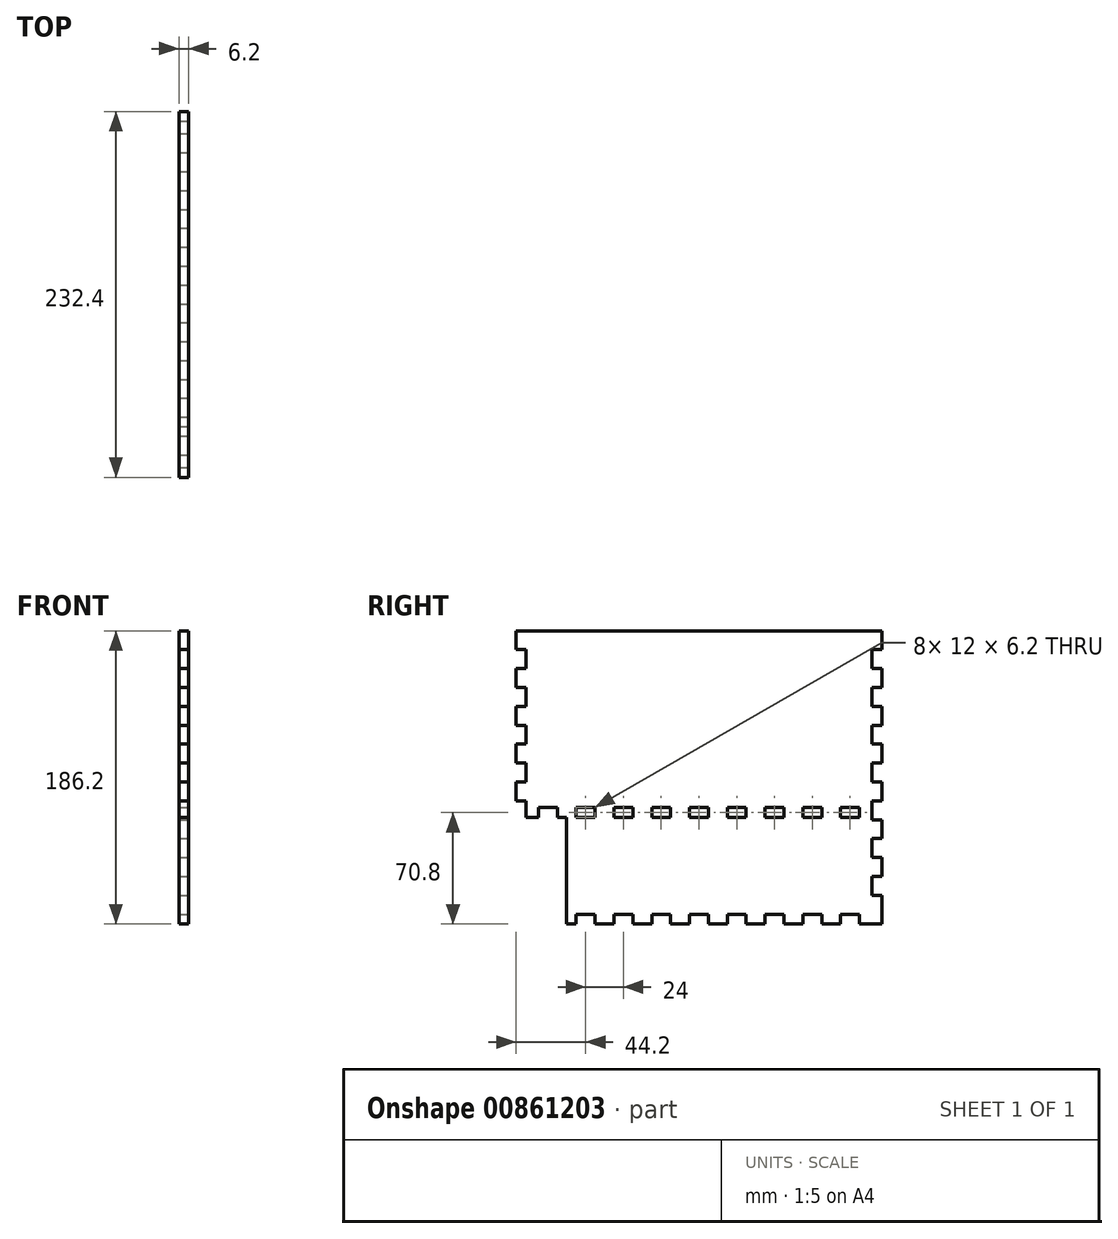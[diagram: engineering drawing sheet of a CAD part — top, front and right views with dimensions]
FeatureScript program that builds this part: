
annotation { "Feature Type Name" : "Feature", "Feature Type Description" : "" }
export const myFeature = defineFeature(function(context is Context, id is Id, definition is map)
    precondition{}
    {
        {
            var Q0;
            Q0=qCreatedBy(makeId("Right.planeOp"),FACE);
            var sketch = newSketch(context, id + "F0", { "sketchPlane" : qUnion([Q0])});
            skLineSegment(sketch, "E0.bottom", {"start": v(110, 90) * mm, "end": v(-110, 90) * mm});
            skLineSegment(sketch, "E0.top", {"start": v(110, -90) * mm, "end": v(-110, -90) * mm});
            skLineSegment(sketch, "E0.left", {"start": v(110, 90) * mm, "end": v(110, -90) * mm});
            skLineSegment(sketch, "E0.right", {"start": v(-110, 90) * mm, "end": v(-110, -90) * mm});
            skPoint(sketch, "E0.middle", {"position": v(0, 0) * mm});
            skSolve(sketch);
        }
        {
            var Q0;
            Q0=makeQuery(id+"F0.imprint","IMPRINT",FACE,{"disambiguationData":[TD([[makeQuery(id+"F0.imprint","IMPRINT",EDGE,{"derivedFrom":sQuery(id+"F0.wireOp",EDGE,"E0.bottom")}),1.0]])]});
            extrude(context, id + "F1", {"entities" : qUnion([Q0]), "depth" : 6.2 * mm, "offsetDistance" : 25 * mm});
        }
        {
            var Q0;
            Q0=makeQuery(id+"F1.opExtrude","CAP_FACE",FACE,{"disambiguationData":[OSD([sQuery(id+"F0.wireOp",EDGE,"E0.bottom"),sQuery(id+"F0.wireOp",EDGE,"E0.top"),sQuery(id+"F0.wireOp",EDGE,"E0.left"),sQuery(id+"F0.wireOp",EDGE,"E0.right")])],"isStart":false});
            var sketch = newSketch(context, id + "F2", { "sketchPlane" : qUnion([Q0])});
            skLineSegment(sketch, "E1", {"start": v(-110, -90) * mm, "end": v(-110, -28.5) * mm, "construction": true});
            skLineSegment(sketch, "E2", {"start": v(-110, -28.5) * mm, "end": v(0, -28.5) * mm, "construction": true});
            skLineSegment(sketch, "E3", {"start": v(0, -28.5) * mm, "end": v(0, -22.3) * mm, "construction": true});
            skPoint(sketch, "E4.orphan", {"position": v(110, -28.5) * mm});
            skLineSegment(sketch, "E5.bottom", {"start": v(6, -22.3) * mm, "end": v(-6, -22.3) * mm});
            skLineSegment(sketch, "E5.top", {"start": v(6, -28.5) * mm, "end": v(-6, -28.5) * mm});
            skLineSegment(sketch, "E5.left", {"start": v(6, -22.3) * mm, "end": v(6, -28.5) * mm});
            skLineSegment(sketch, "E5.right", {"start": v(-6, -22.3) * mm, "end": v(-6, -28.5) * mm});
            skPoint(sketch, "E5.middle", {"position": v(0, -25.4) * mm});
            skLineSegment(sketch, "E6.1.0.0", {"start": v(30, -28.5) * mm, "end": v(18, -28.5) * mm});
            skLineSegment(sketch, "E6.1.0.1", {"start": v(30, -22.3) * mm, "end": v(30, -28.5) * mm});
            skLineSegment(sketch, "E6.1.0.2", {"start": v(30, -22.3) * mm, "end": v(18, -22.3) * mm});
            skLineSegment(sketch, "E6.1.0.3", {"start": v(18, -22.3) * mm, "end": v(18, -28.5) * mm});
            skLineSegment(sketch, "E6.2.0.0", {"start": v(54, -28.5) * mm, "end": v(42, -28.5) * mm});
            skLineSegment(sketch, "E6.2.0.1", {"start": v(54, -22.3) * mm, "end": v(54, -28.5) * mm});
            skLineSegment(sketch, "E6.2.0.2", {"start": v(54, -22.3) * mm, "end": v(42, -22.3) * mm});
            skLineSegment(sketch, "E6.2.0.3", {"start": v(42, -22.3) * mm, "end": v(42, -28.5) * mm});
            skLineSegment(sketch, "E6.3.0.0", {"start": v(78, -28.5) * mm, "end": v(66, -28.5) * mm});
            skLineSegment(sketch, "E6.3.0.1", {"start": v(78, -22.3) * mm, "end": v(78, -28.5) * mm});
            skLineSegment(sketch, "E6.3.0.2", {"start": v(78, -22.3) * mm, "end": v(66, -22.3) * mm});
            skLineSegment(sketch, "E6.3.0.3", {"start": v(66, -22.3) * mm, "end": v(66, -28.5) * mm});
            skLineSegment(sketch, "E6.4.0.0", {"start": v(102, -28.5) * mm, "end": v(90, -28.5) * mm});
            skLineSegment(sketch, "E6.4.0.1", {"start": v(102, -22.3) * mm, "end": v(102, -28.5) * mm});
            skLineSegment(sketch, "E6.4.0.2", {"start": v(102, -22.3) * mm, "end": v(90, -22.3) * mm});
            skLineSegment(sketch, "E6.4.0.3", {"start": v(90, -22.3) * mm, "end": v(90, -28.5) * mm});
            skLineSegment(sketch, "E6.direction1", {"start": v(-6, -28.5) * mm, "end": v(18, -28.5) * mm, "construction": true});
            skLineSegment(sketch, "E7.MirrorCS", {"start": v(-78, -22.3) * mm, "end": v(-78, -28.5) * mm});
            skLineSegment(sketch, "E8.MirrorCS", {"start": v(-66, -22.3) * mm, "end": v(-66, -28.5) * mm});
            skLineSegment(sketch, "E9.MirrorCS", {"start": v(-102, -22.3) * mm, "end": v(-102, -28.5) * mm});
            skLineSegment(sketch, "E10.MirrorCS", {"start": v(-30, -22.3) * mm, "end": v(-30, -28.5) * mm});
            skLineSegment(sketch, "E11.MirrorCS", {"start": v(-42, -22.3) * mm, "end": v(-42, -28.5) * mm});
            skLineSegment(sketch, "E12.MirrorCS", {"start": v(-18, -22.3) * mm, "end": v(-18, -28.5) * mm});
            skLineSegment(sketch, "E13.MirrorCS", {"start": v(-54, -22.3) * mm, "end": v(-54, -28.5) * mm});
            skLineSegment(sketch, "E14.MirrorCS", {"start": v(-90, -22.3) * mm, "end": v(-90, -28.5) * mm});
            skLineSegment(sketch, "E15.MirrorCS", {"start": v(-78, -22.3) * mm, "end": v(-66, -22.3) * mm});
            skLineSegment(sketch, "E16.MirrorCS", {"start": v(-102, -28.5) * mm, "end": v(-90, -28.5) * mm});
            skLineSegment(sketch, "E17.MirrorCS", {"start": v(-102, -22.3) * mm, "end": v(-90, -22.3) * mm});
            skLineSegment(sketch, "E18.MirrorCS", {"start": v(-30, -28.5) * mm, "end": v(-18, -28.5) * mm});
            skLineSegment(sketch, "E19.MirrorCS", {"start": v(-54, -22.3) * mm, "end": v(-42, -22.3) * mm});
            skLineSegment(sketch, "E20.MirrorCS", {"start": v(-54, -28.5) * mm, "end": v(-42, -28.5) * mm});
            skLineSegment(sketch, "E21.MirrorCS", {"start": v(-30, -22.3) * mm, "end": v(-18, -22.3) * mm});
            skLineSegment(sketch, "E22.MirrorCS", {"start": v(-78, -28.5) * mm, "end": v(-66, -28.5) * mm});
            skSolve(sketch);
        }
        {
            var Q0;
            Q0=makeQuery(id+"F2.imprint","IMPRINT",FACE,{"disambiguationData":[TD([[makeQuery(id+"F2.imprint","IMPRINT",EDGE,{"derivedFrom":sQuery(id+"F2.wireOp",EDGE,"E9.MirrorCS")}),1.0]])]});
            var Q1;
            Q1=makeQuery(id+"F2.imprint","IMPRINT",FACE,{"disambiguationData":[TD([[makeQuery(id+"F2.imprint","IMPRINT",EDGE,{"derivedFrom":sQuery(id+"F2.wireOp",EDGE,"E7.MirrorCS")}),1.0]])]});
            var Q2;
            Q2=makeQuery(id+"F2.imprint","IMPRINT",FACE,{"disambiguationData":[TD([[makeQuery(id+"F2.imprint","IMPRINT",EDGE,{"derivedFrom":sQuery(id+"F2.wireOp",EDGE,"E11.MirrorCS")}),-1.0]])]});
            var Q3;
            Q3=makeQuery(id+"F2.imprint","IMPRINT",FACE,{"disambiguationData":[TD([[makeQuery(id+"F2.imprint","IMPRINT",EDGE,{"derivedFrom":sQuery(id+"F2.wireOp",EDGE,"E10.MirrorCS")}),1.0]])]});
            var Q4;
            Q4=makeQuery(id+"F2.imprint","IMPRINT",FACE,{"disambiguationData":[TD([[makeQuery(id+"F2.imprint","IMPRINT",EDGE,{"derivedFrom":sQuery(id+"F2.wireOp",EDGE,"E5.bottom")}),1.0]])]});
            var Q5;
            Q5=makeQuery(id+"F2.imprint","IMPRINT",FACE,{"disambiguationData":[TD([[makeQuery(id+"F2.imprint","IMPRINT",EDGE,{"derivedFrom":sQuery(id+"F2.wireOp",EDGE,"E6.1.0.0")}),-1.0]])]});
            var Q6;
            Q6=makeQuery(id+"F2.imprint","IMPRINT",FACE,{"disambiguationData":[TD([[makeQuery(id+"F2.imprint","IMPRINT",EDGE,{"derivedFrom":sQuery(id+"F2.wireOp",EDGE,"E6.2.0.0")}),-1.0]])]});
            var Q7;
            Q7=makeQuery(id+"F2.imprint","IMPRINT",FACE,{"disambiguationData":[TD([[makeQuery(id+"F2.imprint","IMPRINT",EDGE,{"derivedFrom":sQuery(id+"F2.wireOp",EDGE,"E6.3.0.0")}),-1.0]])]});
            var Q8;
            Q8=makeQuery(id+"F2.imprint","IMPRINT",FACE,{"disambiguationData":[TD([[makeQuery(id+"F2.imprint","IMPRINT",EDGE,{"derivedFrom":sQuery(id+"F2.wireOp",EDGE,"E6.4.0.0")}),-1.0]])]});
            extrude(context, id + "F3", {"entities" : qUnion([Q0, Q1, Q2, Q3, Q4, Q5, Q6, Q7, Q8]), "operationType" : NewBodyOperationType.REMOVE, "endBound" : BoundingType.THROUGH_ALL, "oppositeDirection" : true, "depth" : 25 * mm, "offsetDistance" : 25 * mm});
        }
        {
            var Q0;
            Q0=makeQuery(id+"F1.opExtrude","CAP_FACE",FACE,{"disambiguationData":[OSD([sQuery(id+"F0.wireOp",EDGE,"E0.bottom"),sQuery(id+"F0.wireOp",EDGE,"E0.top"),sQuery(id+"F0.wireOp",EDGE,"E0.left"),sQuery(id+"F0.wireOp",EDGE,"E0.right")])],"isStart":false});
            var sketch = newSketch(context, id + "F4", { "sketchPlane" : qUnion([Q0])});
            skPoint(sketch, "E23.start.orphan", {"position": v(-86, -28.5) * mm});
            skLineSegment(sketch, "E24", {"start": v(-90, -28.5) * mm, "end": v(-78, -28.5) * mm, "construction": true});
            skLineSegment(sketch, "E25.bottom", {"start": v(-84, -28.5) * mm, "end": v(-110, -28.5) * mm});
            skLineSegment(sketch, "E25.top", {"start": v(-84, -90) * mm, "end": v(-110, -90) * mm});
            skLineSegment(sketch, "E25.left", {"start": v(-84, -28.5) * mm, "end": v(-84, -90) * mm});
            skLineSegment(sketch, "E25.right", {"start": v(-110, -28.5) * mm, "end": v(-110, -90) * mm});
            skSolve(sketch);
        }
        {
            var Q0;
            Q0=makeQuery(id+"F4.imprint","IMPRINT",FACE,{"disambiguationData":[TD([[makeQuery(id+"F4.imprint","IMPRINT",EDGE,{"derivedFrom":sQuery(id+"F4.wireOp",EDGE,"E25.top")}),-1.0]])]});
            extrude(context, id + "F5", {"entities" : qUnion([Q0]), "operationType" : NewBodyOperationType.REMOVE, "endBound" : BoundingType.THROUGH_ALL, "oppositeDirection" : true, "depth" : 25 * mm, "offsetDistance" : 25 * mm});
        }
        {
            var Q0;
            Q0=makeQuery(id+"F1.opExtrude","CAP_FACE",FACE,{"disambiguationData":[OSD([sQuery(id+"F0.wireOp",EDGE,"E0.bottom"),sQuery(id+"F0.wireOp",EDGE,"E0.top"),sQuery(id+"F0.wireOp",EDGE,"E0.left"),sQuery(id+"F0.wireOp",EDGE,"E0.right")])],"isStart":false});
            var sketch = newSketch(context, id + "F6", { "sketchPlane" : qUnion([Q0])});
            skLineSegment(sketch, "E26", {"start": v(0, 0) * mm, "end": v(110, 0) * mm, "construction": true});
            skLineSegment(sketch, "E27", {"start": v(110, 0) * mm, "end": v(110, 6) * mm, "construction": true});
            skLineSegment(sketch, "E28.bottom", {"start": v(110, 6) * mm, "end": v(116.2, 6) * mm});
            skLineSegment(sketch, "E28.top", {"start": v(110, 18) * mm, "end": v(116.2, 18) * mm});
            skLineSegment(sketch, "E28.left", {"start": v(110, 6) * mm, "end": v(110, 18) * mm});
            skLineSegment(sketch, "E28.right", {"start": v(116.2, 6) * mm, "end": v(116.2, 18) * mm});
            skLineSegment(sketch, "E29.0.1.0", {"start": v(116.2, 30) * mm, "end": v(116.2, 42) * mm});
            skLineSegment(sketch, "E29.0.1.1", {"start": v(110, 42) * mm, "end": v(116.2, 42) * mm});
            skLineSegment(sketch, "E29.0.1.2", {"start": v(110, 30) * mm, "end": v(110, 42) * mm});
            skLineSegment(sketch, "E29.0.1.3", {"start": v(110, 30) * mm, "end": v(116.2, 30) * mm});
            skLineSegment(sketch, "E29.0.2.0", {"start": v(116.2, 54) * mm, "end": v(116.2, 66) * mm});
            skLineSegment(sketch, "E29.0.2.1", {"start": v(110, 66) * mm, "end": v(116.2, 66) * mm});
            skLineSegment(sketch, "E29.0.2.2", {"start": v(110, 54) * mm, "end": v(110, 66) * mm});
            skLineSegment(sketch, "E29.0.2.3", {"start": v(110, 54) * mm, "end": v(116.2, 54) * mm});
            skLineSegment(sketch, "E29.0.3.0", {"start": v(116.2, 78) * mm, "end": v(116.2, 90) * mm});
            skLineSegment(sketch, "E29.0.3.1", {"start": v(110, 90) * mm, "end": v(116.2, 90) * mm});
            skLineSegment(sketch, "E29.0.3.2", {"start": v(110, 78) * mm, "end": v(110, 90) * mm});
            skLineSegment(sketch, "E29.0.3.3", {"start": v(110, 78) * mm, "end": v(116.2, 78) * mm});
            skLineSegment(sketch, "E29.direction1", {"start": v(116.2, 6) * mm, "end": v(141.2, 6) * mm, "construction": true});
            skLineSegment(sketch, "E29.direction2", {"start": v(116.2, 6) * mm, "end": v(116.2, 30) * mm, "construction": true});
            skLineSegment(sketch, "E30.MirrorCS", {"start": v(116.2, -6) * mm, "end": v(116.2, -18) * mm});
            skLineSegment(sketch, "E31.MirrorCS", {"start": v(110, -42) * mm, "end": v(116.2, -42) * mm});
            skLineSegment(sketch, "E32.MirrorCS", {"start": v(116.2, -6) * mm, "end": v(116.2, -30) * mm, "construction": true});
            skLineSegment(sketch, "E33.MirrorCS", {"start": v(116.2, -30) * mm, "end": v(116.2, -42) * mm});
            skLineSegment(sketch, "E34.MirrorCS", {"start": v(110, -54) * mm, "end": v(110, -66) * mm});
            skLineSegment(sketch, "E35.MirrorCS", {"start": v(116.2, -78) * mm, "end": v(116.2, -90) * mm});
            skLineSegment(sketch, "E36.MirrorCS", {"start": v(110, -66) * mm, "end": v(116.2, -66) * mm});
            skLineSegment(sketch, "E37.MirrorCS", {"start": v(110, -54) * mm, "end": v(116.2, -54) * mm});
            skLineSegment(sketch, "E38.MirrorCS", {"start": v(110, -18) * mm, "end": v(116.2, -18) * mm});
            skLineSegment(sketch, "E39.MirrorCS", {"start": v(110, -6) * mm, "end": v(110, -18) * mm});
            skLineSegment(sketch, "E40.MirrorCS", {"start": v(110, -90) * mm, "end": v(116.2, -90) * mm});
            skLineSegment(sketch, "E41.MirrorCS", {"start": v(110, -78) * mm, "end": v(116.2, -78) * mm});
            skLineSegment(sketch, "E42.MirrorCS", {"start": v(110, -6) * mm, "end": v(116.2, -6) * mm});
            skLineSegment(sketch, "E43.MirrorCS", {"start": v(116.2, -54) * mm, "end": v(116.2, -66) * mm});
            skLineSegment(sketch, "E44.MirrorCS", {"start": v(110, -30) * mm, "end": v(116.2, -30) * mm});
            skLineSegment(sketch, "E45.MirrorCS", {"start": v(110, -30) * mm, "end": v(110, -42) * mm});
            skLineSegment(sketch, "E46.MirrorCS", {"start": v(110, -78) * mm, "end": v(110, -90) * mm});
            skLineSegment(sketch, "E47.MirrorCS", {"start": v(-110, 0) * mm, "end": v(-110, 6) * mm, "construction": true});
            skLineSegment(sketch, "E48.MirrorCS", {"start": v(-110, 6) * mm, "end": v(-116.2, 6) * mm});
            skLineSegment(sketch, "E49.MirrorCS", {"start": v(-110, -6) * mm, "end": v(-116.2, -6) * mm});
            skLineSegment(sketch, "E50.MirrorCS", {"start": v(-110, 30) * mm, "end": v(-116.2, 30) * mm});
            skLineSegment(sketch, "E51.MirrorCS", {"start": v(-110, 42) * mm, "end": v(-116.2, 42) * mm});
            skLineSegment(sketch, "E52.MirrorCS", {"start": v(-116.2, 6) * mm, "end": v(-116.2, 30) * mm, "construction": true});
            skLineSegment(sketch, "E53.MirrorCS", {"start": v(-116.2, 30) * mm, "end": v(-116.2, 42) * mm});
            skLineSegment(sketch, "E54.MirrorCS", {"start": v(-116.2, -6) * mm, "end": v(-116.2, -18) * mm});
            skLineSegment(sketch, "E55.MirrorCS", {"start": v(-110, -6) * mm, "end": v(-110, -18) * mm});
            skLineSegment(sketch, "E56.MirrorCS", {"start": v(-116.2, 6) * mm, "end": v(-116.2, 18) * mm});
            skLineSegment(sketch, "E57.MirrorCS", {"start": v(-110, 30) * mm, "end": v(-110, 42) * mm});
            skLineSegment(sketch, "E58.MirrorCS", {"start": v(-116.2, 78) * mm, "end": v(-116.2, 90) * mm});
            skLineSegment(sketch, "E59.MirrorCS", {"start": v(-110, 54) * mm, "end": v(-116.2, 54) * mm});
            skLineSegment(sketch, "E60.MirrorCS", {"start": v(-110, 66) * mm, "end": v(-116.2, 66) * mm});
            skLineSegment(sketch, "E61.MirrorCS", {"start": v(-116.2, 54) * mm, "end": v(-116.2, 66) * mm});
            skLineSegment(sketch, "E62.MirrorCS", {"start": v(-110, -18) * mm, "end": v(-116.2, -18) * mm});
            skLineSegment(sketch, "E63.MirrorCS", {"start": v(-110, 18) * mm, "end": v(-116.2, 18) * mm});
            skLineSegment(sketch, "E64.MirrorCS", {"start": v(-110, 54) * mm, "end": v(-110, 66) * mm});
            skLineSegment(sketch, "E65.MirrorCS", {"start": v(-116.2, -6) * mm, "end": v(-116.2, -30) * mm, "construction": true});
            skLineSegment(sketch, "E66.MirrorCS", {"start": v(-110, 78) * mm, "end": v(-110, 90) * mm});
            skLineSegment(sketch, "E67.MirrorCS", {"start": v(-110, 6) * mm, "end": v(-110, 18) * mm});
            skLineSegment(sketch, "E68.MirrorCS", {"start": v(-110, 90) * mm, "end": v(-116.2, 90) * mm});
            skLineSegment(sketch, "E69.MirrorCS", {"start": v(-110, 78) * mm, "end": v(-116.2, 78) * mm});
            skLineSegment(sketch, "E70.MirrorCS", {"start": v(-116.2, 6) * mm, "end": v(-141.2, 6) * mm, "construction": true});
            skPoint(sketch, "E71.MirrorCS.start.orphan", {"position": v(-110, -30) * mm});
            skPoint(sketch, "E72.MirrorCS.end.orphan", {"position": v(-116.2, -42) * mm});
            skPoint(sketch, "E72.MirrorCS.start.orphan", {"position": v(-110, -42) * mm});
            skSolve(sketch);
        }
        {
            var Q0;
            Q0 = qSketchRegion(id + "F6", true);
            extrude(context, id + "F7", {"entities" : qUnion([Q0]), "operationType" : NewBodyOperationType.ADD, "oppositeDirection" : true, "depth" : 6.2 * mm, "offsetDistance" : 25 * mm});
        }
        {
            var Q0;
            Q0=makeQuery(id+"F7.boolean.opBoolean","MERGE",FACE,{"derivedFrom":[makeQuery(id+"F1.opExtrude","CAP_FACE",FACE,{"disambiguationData":[OSD([sQuery(id+"F0.wireOp",EDGE,"E0.bottom"),sQuery(id+"F0.wireOp",EDGE,"E0.top"),sQuery(id+"F0.wireOp",EDGE,"E0.left"),sQuery(id+"F0.wireOp",EDGE,"E0.right")])],"isStart":false}),makeQuery(id+"F7.opExtrude","CAP_FACE",FACE,{"disambiguationData":[OSD([sQuery(id+"F6.wireOp",EDGE,"E28.bottom"),sQuery(id+"F6.wireOp",EDGE,"E28.top"),sQuery(id+"F6.wireOp",EDGE,"E28.left"),sQuery(id+"F6.wireOp",EDGE,"E28.right")])],"isStart":true}),makeQuery(id+"F7.opExtrude","CAP_FACE",FACE,{"disambiguationData":[OSD([sQuery(id+"F6.wireOp",EDGE,"E29.0.1.0"),sQuery(id+"F6.wireOp",EDGE,"E29.0.1.1"),sQuery(id+"F6.wireOp",EDGE,"E29.0.1.2"),sQuery(id+"F6.wireOp",EDGE,"E29.0.1.3")])],"isStart":true}),makeQuery(id+"F7.opExtrude","CAP_FACE",FACE,{"disambiguationData":[OSD([sQuery(id+"F6.wireOp",EDGE,"E29.0.2.0"),sQuery(id+"F6.wireOp",EDGE,"E29.0.2.1"),sQuery(id+"F6.wireOp",EDGE,"E29.0.2.2"),sQuery(id+"F6.wireOp",EDGE,"E29.0.2.3")])],"isStart":true}),makeQuery(id+"F7.opExtrude","CAP_FACE",FACE,{"disambiguationData":[OSD([sQuery(id+"F6.wireOp",EDGE,"E29.0.3.0"),sQuery(id+"F6.wireOp",EDGE,"E29.0.3.1"),sQuery(id+"F6.wireOp",EDGE,"E29.0.3.2"),sQuery(id+"F6.wireOp",EDGE,"E29.0.3.3")])],"isStart":true}),makeQuery(id+"F7.opExtrude","CAP_FACE",FACE,{"disambiguationData":[OSD([sQuery(id+"F6.wireOp",EDGE,"E30.MirrorCS"),sQuery(id+"F6.wireOp",EDGE,"E38.MirrorCS"),sQuery(id+"F6.wireOp",EDGE,"E39.MirrorCS"),sQuery(id+"F6.wireOp",EDGE,"E42.MirrorCS")])],"isStart":true}),makeQuery(id+"F7.opExtrude","CAP_FACE",FACE,{"disambiguationData":[OSD([sQuery(id+"F6.wireOp",EDGE,"E31.MirrorCS"),sQuery(id+"F6.wireOp",EDGE,"E33.MirrorCS"),sQuery(id+"F6.wireOp",EDGE,"E44.MirrorCS"),sQuery(id+"F6.wireOp",EDGE,"E45.MirrorCS")])],"isStart":true}),makeQuery(id+"F7.opExtrude","CAP_FACE",FACE,{"disambiguationData":[OSD([sQuery(id+"F6.wireOp",EDGE,"E34.MirrorCS"),sQuery(id+"F6.wireOp",EDGE,"E36.MirrorCS"),sQuery(id+"F6.wireOp",EDGE,"E37.MirrorCS"),sQuery(id+"F6.wireOp",EDGE,"E43.MirrorCS")])],"isStart":true}),makeQuery(id+"F7.opExtrude","CAP_FACE",FACE,{"disambiguationData":[OSD([sQuery(id+"F6.wireOp",EDGE,"E35.MirrorCS"),sQuery(id+"F6.wireOp",EDGE,"E40.MirrorCS"),sQuery(id+"F6.wireOp",EDGE,"E41.MirrorCS"),sQuery(id+"F6.wireOp",EDGE,"E46.MirrorCS")])],"isStart":true}),makeQuery(id+"F7.opExtrude","CAP_FACE",FACE,{"disambiguationData":[OSD([sQuery(id+"F6.wireOp",EDGE,"E48.MirrorCS"),sQuery(id+"F6.wireOp",EDGE,"E56.MirrorCS"),sQuery(id+"F6.wireOp",EDGE,"E63.MirrorCS"),sQuery(id+"F6.wireOp",EDGE,"E67.MirrorCS")])],"isStart":true}),makeQuery(id+"F7.opExtrude","CAP_FACE",FACE,{"disambiguationData":[OSD([sQuery(id+"F6.wireOp",EDGE,"E49.MirrorCS"),sQuery(id+"F6.wireOp",EDGE,"E54.MirrorCS"),sQuery(id+"F6.wireOp",EDGE,"E55.MirrorCS"),sQuery(id+"F6.wireOp",EDGE,"E62.MirrorCS")])],"isStart":true}),makeQuery(id+"F7.opExtrude","CAP_FACE",FACE,{"disambiguationData":[OSD([sQuery(id+"F6.wireOp",EDGE,"E50.MirrorCS"),sQuery(id+"F6.wireOp",EDGE,"E51.MirrorCS"),sQuery(id+"F6.wireOp",EDGE,"E53.MirrorCS"),sQuery(id+"F6.wireOp",EDGE,"E57.MirrorCS")])],"isStart":true}),makeQuery(id+"F7.opExtrude","CAP_FACE",FACE,{"disambiguationData":[OSD([sQuery(id+"F6.wireOp",EDGE,"E58.MirrorCS"),sQuery(id+"F6.wireOp",EDGE,"E66.MirrorCS"),sQuery(id+"F6.wireOp",EDGE,"E68.MirrorCS"),sQuery(id+"F6.wireOp",EDGE,"E69.MirrorCS")])],"isStart":true}),makeQuery(id+"F7.opExtrude","CAP_FACE",FACE,{"disambiguationData":[OSD([sQuery(id+"F6.wireOp",EDGE,"E59.MirrorCS"),sQuery(id+"F6.wireOp",EDGE,"E60.MirrorCS"),sQuery(id+"F6.wireOp",EDGE,"E61.MirrorCS"),sQuery(id+"F6.wireOp",EDGE,"E64.MirrorCS")])],"isStart":true})]});
            var sketch = newSketch(context, id + "F8", { "sketchPlane" : qUnion([Q0])});
            skLineSegment(sketch, "E73.bottom", {"start": v(-84, -90) * mm, "end": v(-78, -90) * mm});
            skLineSegment(sketch, "E73.top", {"start": v(-84, -96.2) * mm, "end": v(-78, -96.2) * mm});
            skLineSegment(sketch, "E73.left", {"start": v(-84, -90) * mm, "end": v(-84, -96.2) * mm});
            skLineSegment(sketch, "E73.right", {"start": v(-78, -90) * mm, "end": v(-78, -96.2) * mm});
            skLineSegment(sketch, "E74", {"start": v(-78, -90) * mm, "end": v(-66, -90) * mm, "construction": true});
            skLineSegment(sketch, "E75.bottom", {"start": v(-66, -90) * mm, "end": v(-54, -90) * mm});
            skLineSegment(sketch, "E75.top", {"start": v(-66, -96.2) * mm, "end": v(-54, -96.2) * mm});
            skLineSegment(sketch, "E75.left", {"start": v(-66, -90) * mm, "end": v(-66, -96.2) * mm});
            skLineSegment(sketch, "E75.right", {"start": v(-54, -90) * mm, "end": v(-54, -96.2) * mm});
            skLineSegment(sketch, "E76.1.0.0", {"start": v(-42, -96.2) * mm, "end": v(-30, -96.2) * mm});
            skLineSegment(sketch, "E76.1.0.1", {"start": v(-30, -90) * mm, "end": v(-30, -96.2) * mm});
            skLineSegment(sketch, "E76.1.0.2", {"start": v(-42, -90) * mm, "end": v(-30, -90) * mm});
            skLineSegment(sketch, "E76.1.0.3", {"start": v(-42, -90) * mm, "end": v(-42, -96.2) * mm});
            skLineSegment(sketch, "E76.1.0.4", {"start": v(-54, -90) * mm, "end": v(-42, -90) * mm, "construction": true});
            skLineSegment(sketch, "E76.2.0.0", {"start": v(-18, -96.2) * mm, "end": v(-6, -96.2) * mm});
            skLineSegment(sketch, "E76.2.0.1", {"start": v(-6, -90) * mm, "end": v(-6, -96.2) * mm});
            skLineSegment(sketch, "E76.2.0.2", {"start": v(-18, -90) * mm, "end": v(-6, -90) * mm});
            skLineSegment(sketch, "E76.2.0.3", {"start": v(-18, -90) * mm, "end": v(-18, -96.2) * mm});
            skLineSegment(sketch, "E76.2.0.4", {"start": v(-30, -90) * mm, "end": v(-18, -90) * mm, "construction": true});
            skLineSegment(sketch, "E76.3.0.0", {"start": v(6, -96.2) * mm, "end": v(18, -96.2) * mm});
            skLineSegment(sketch, "E76.3.0.1", {"start": v(18, -90) * mm, "end": v(18, -96.2) * mm});
            skLineSegment(sketch, "E76.3.0.2", {"start": v(6, -90) * mm, "end": v(18, -90) * mm});
            skLineSegment(sketch, "E76.3.0.3", {"start": v(6, -90) * mm, "end": v(6, -96.2) * mm});
            skLineSegment(sketch, "E76.3.0.4", {"start": v(-6, -90) * mm, "end": v(6, -90) * mm, "construction": true});
            skLineSegment(sketch, "E76.4.0.0", {"start": v(30, -96.2) * mm, "end": v(42, -96.2) * mm});
            skLineSegment(sketch, "E76.4.0.1", {"start": v(42, -90) * mm, "end": v(42, -96.2) * mm});
            skLineSegment(sketch, "E76.4.0.2", {"start": v(30, -90) * mm, "end": v(42, -90) * mm});
            skLineSegment(sketch, "E76.4.0.3", {"start": v(30, -90) * mm, "end": v(30, -96.2) * mm});
            skLineSegment(sketch, "E76.4.0.4", {"start": v(18, -90) * mm, "end": v(30, -90) * mm, "construction": true});
            skLineSegment(sketch, "E76.5.0.0", {"start": v(54, -96.2) * mm, "end": v(66, -96.2) * mm});
            skLineSegment(sketch, "E76.5.0.1", {"start": v(66, -90) * mm, "end": v(66, -96.2) * mm});
            skLineSegment(sketch, "E76.5.0.2", {"start": v(54, -90) * mm, "end": v(66, -90) * mm});
            skLineSegment(sketch, "E76.5.0.3", {"start": v(54, -90) * mm, "end": v(54, -96.2) * mm});
            skLineSegment(sketch, "E76.5.0.4", {"start": v(42, -90) * mm, "end": v(54, -90) * mm, "construction": true});
            skLineSegment(sketch, "E76.6.0.0", {"start": v(78, -96.2) * mm, "end": v(90, -96.2) * mm});
            skLineSegment(sketch, "E76.6.0.1", {"start": v(90, -90) * mm, "end": v(90, -96.2) * mm});
            skLineSegment(sketch, "E76.6.0.2", {"start": v(78, -90) * mm, "end": v(90, -90) * mm});
            skLineSegment(sketch, "E76.6.0.3", {"start": v(78, -90) * mm, "end": v(78, -96.2) * mm});
            skLineSegment(sketch, "E76.6.0.4", {"start": v(66, -90) * mm, "end": v(78, -90) * mm, "construction": true});
            skLineSegment(sketch, "E76.7.0.0", {"start": v(102, -96.2) * mm, "end": v(114, -96.2) * mm});
            skLineSegment(sketch, "E76.7.0.1", {"start": v(114, -90) * mm, "end": v(114, -96.2) * mm});
            skLineSegment(sketch, "E76.7.0.2", {"start": v(102, -90) * mm, "end": v(114, -90) * mm});
            skLineSegment(sketch, "E76.7.0.3", {"start": v(102, -90) * mm, "end": v(102, -96.2) * mm});
            skLineSegment(sketch, "E76.7.0.4", {"start": v(90, -90) * mm, "end": v(102, -90) * mm, "construction": true});
            skLineSegment(sketch, "E76.direction1", {"start": v(-78, -90) * mm, "end": v(-54, -90) * mm, "construction": true});
            skSolve(sketch);
        }
        {
            var Q0;
            Q0 = qSketchRegion(id + "F8", true);
            extrude(context, id + "F9", {"entities" : qUnion([Q0]), "operationType" : NewBodyOperationType.ADD, "oppositeDirection" : true, "depth" : 6.2 * mm, "offsetDistance" : 25 * mm});
        }
        {
            var Q0;
            Q0=makeQuery(id+"F9.boolean.opBoolean","MERGE",FACE,{"derivedFrom":[makeQuery(id+"F7.boolean.opBoolean","MERGE",FACE,{"derivedFrom":[makeQuery(id+"F1.opExtrude","CAP_FACE",FACE,{"disambiguationData":[OSD([sQuery(id+"F0.wireOp",EDGE,"E0.bottom"),sQuery(id+"F0.wireOp",EDGE,"E0.top"),sQuery(id+"F0.wireOp",EDGE,"E0.left"),sQuery(id+"F0.wireOp",EDGE,"E0.right")])],"isStart":false}),makeQuery(id+"F7.opExtrude","CAP_FACE",FACE,{"disambiguationData":[OSD([sQuery(id+"F6.wireOp",EDGE,"E28.bottom"),sQuery(id+"F6.wireOp",EDGE,"E28.top"),sQuery(id+"F6.wireOp",EDGE,"E28.left"),sQuery(id+"F6.wireOp",EDGE,"E28.right")])],"isStart":true}),makeQuery(id+"F7.opExtrude","CAP_FACE",FACE,{"disambiguationData":[OSD([sQuery(id+"F6.wireOp",EDGE,"E29.0.1.0"),sQuery(id+"F6.wireOp",EDGE,"E29.0.1.1"),sQuery(id+"F6.wireOp",EDGE,"E29.0.1.2"),sQuery(id+"F6.wireOp",EDGE,"E29.0.1.3")])],"isStart":true}),makeQuery(id+"F7.opExtrude","CAP_FACE",FACE,{"disambiguationData":[OSD([sQuery(id+"F6.wireOp",EDGE,"E29.0.2.0"),sQuery(id+"F6.wireOp",EDGE,"E29.0.2.1"),sQuery(id+"F6.wireOp",EDGE,"E29.0.2.2"),sQuery(id+"F6.wireOp",EDGE,"E29.0.2.3")])],"isStart":true}),makeQuery(id+"F7.opExtrude","CAP_FACE",FACE,{"disambiguationData":[OSD([sQuery(id+"F6.wireOp",EDGE,"E29.0.3.0"),sQuery(id+"F6.wireOp",EDGE,"E29.0.3.1"),sQuery(id+"F6.wireOp",EDGE,"E29.0.3.2"),sQuery(id+"F6.wireOp",EDGE,"E29.0.3.3")])],"isStart":true}),makeQuery(id+"F7.opExtrude","CAP_FACE",FACE,{"disambiguationData":[OSD([sQuery(id+"F6.wireOp",EDGE,"E30.MirrorCS"),sQuery(id+"F6.wireOp",EDGE,"E38.MirrorCS"),sQuery(id+"F6.wireOp",EDGE,"E39.MirrorCS"),sQuery(id+"F6.wireOp",EDGE,"E42.MirrorCS")])],"isStart":true}),makeQuery(id+"F7.opExtrude","CAP_FACE",FACE,{"disambiguationData":[OSD([sQuery(id+"F6.wireOp",EDGE,"E31.MirrorCS"),sQuery(id+"F6.wireOp",EDGE,"E33.MirrorCS"),sQuery(id+"F6.wireOp",EDGE,"E44.MirrorCS"),sQuery(id+"F6.wireOp",EDGE,"E45.MirrorCS")])],"isStart":true}),makeQuery(id+"F7.opExtrude","CAP_FACE",FACE,{"disambiguationData":[OSD([sQuery(id+"F6.wireOp",EDGE,"E34.MirrorCS"),sQuery(id+"F6.wireOp",EDGE,"E36.MirrorCS"),sQuery(id+"F6.wireOp",EDGE,"E37.MirrorCS"),sQuery(id+"F6.wireOp",EDGE,"E43.MirrorCS")])],"isStart":true}),makeQuery(id+"F7.opExtrude","CAP_FACE",FACE,{"disambiguationData":[OSD([sQuery(id+"F6.wireOp",EDGE,"E35.MirrorCS"),sQuery(id+"F6.wireOp",EDGE,"E40.MirrorCS"),sQuery(id+"F6.wireOp",EDGE,"E41.MirrorCS"),sQuery(id+"F6.wireOp",EDGE,"E46.MirrorCS")])],"isStart":true}),makeQuery(id+"F7.opExtrude","CAP_FACE",FACE,{"disambiguationData":[OSD([sQuery(id+"F6.wireOp",EDGE,"E48.MirrorCS"),sQuery(id+"F6.wireOp",EDGE,"E56.MirrorCS"),sQuery(id+"F6.wireOp",EDGE,"E63.MirrorCS"),sQuery(id+"F6.wireOp",EDGE,"E67.MirrorCS")])],"isStart":true}),makeQuery(id+"F7.opExtrude","CAP_FACE",FACE,{"disambiguationData":[OSD([sQuery(id+"F6.wireOp",EDGE,"E49.MirrorCS"),sQuery(id+"F6.wireOp",EDGE,"E54.MirrorCS"),sQuery(id+"F6.wireOp",EDGE,"E55.MirrorCS"),sQuery(id+"F6.wireOp",EDGE,"E62.MirrorCS")])],"isStart":true}),makeQuery(id+"F7.opExtrude","CAP_FACE",FACE,{"disambiguationData":[OSD([sQuery(id+"F6.wireOp",EDGE,"E50.MirrorCS"),sQuery(id+"F6.wireOp",EDGE,"E51.MirrorCS"),sQuery(id+"F6.wireOp",EDGE,"E53.MirrorCS"),sQuery(id+"F6.wireOp",EDGE,"E57.MirrorCS")])],"isStart":true}),makeQuery(id+"F7.opExtrude","CAP_FACE",FACE,{"disambiguationData":[OSD([sQuery(id+"F6.wireOp",EDGE,"E58.MirrorCS"),sQuery(id+"F6.wireOp",EDGE,"E66.MirrorCS"),sQuery(id+"F6.wireOp",EDGE,"E68.MirrorCS"),sQuery(id+"F6.wireOp",EDGE,"E69.MirrorCS")])],"isStart":true}),makeQuery(id+"F7.opExtrude","CAP_FACE",FACE,{"disambiguationData":[OSD([sQuery(id+"F6.wireOp",EDGE,"E59.MirrorCS"),sQuery(id+"F6.wireOp",EDGE,"E60.MirrorCS"),sQuery(id+"F6.wireOp",EDGE,"E61.MirrorCS"),sQuery(id+"F6.wireOp",EDGE,"E64.MirrorCS")])],"isStart":true})]}),makeQuery(id+"F9.opExtrude","CAP_FACE",FACE,{"disambiguationData":[OSD([sQuery(id+"F8.wireOp",EDGE,"E73.bottom"),sQuery(id+"F8.wireOp",EDGE,"E73.top"),sQuery(id+"F8.wireOp",EDGE,"E73.left"),sQuery(id+"F8.wireOp",EDGE,"E73.right")])],"isStart":true}),makeQuery(id+"F9.opExtrude","CAP_FACE",FACE,{"disambiguationData":[OSD([sQuery(id+"F8.wireOp",EDGE,"E75.bottom"),sQuery(id+"F8.wireOp",EDGE,"E75.top"),sQuery(id+"F8.wireOp",EDGE,"E75.left"),sQuery(id+"F8.wireOp",EDGE,"E75.right")])],"isStart":true}),makeQuery(id+"F9.opExtrude","CAP_FACE",FACE,{"disambiguationData":[OSD([sQuery(id+"F8.wireOp",EDGE,"E76.1.0.0"),sQuery(id+"F8.wireOp",EDGE,"E76.1.0.1"),sQuery(id+"F8.wireOp",EDGE,"E76.1.0.2"),sQuery(id+"F8.wireOp",EDGE,"E76.1.0.3")])],"isStart":true}),makeQuery(id+"F9.opExtrude","CAP_FACE",FACE,{"disambiguationData":[OSD([sQuery(id+"F8.wireOp",EDGE,"E76.2.0.0"),sQuery(id+"F8.wireOp",EDGE,"E76.2.0.1"),sQuery(id+"F8.wireOp",EDGE,"E76.2.0.2"),sQuery(id+"F8.wireOp",EDGE,"E76.2.0.3")])],"isStart":true}),makeQuery(id+"F9.opExtrude","CAP_FACE",FACE,{"disambiguationData":[OSD([sQuery(id+"F8.wireOp",EDGE,"E76.3.0.0"),sQuery(id+"F8.wireOp",EDGE,"E76.3.0.1"),sQuery(id+"F8.wireOp",EDGE,"E76.3.0.2"),sQuery(id+"F8.wireOp",EDGE,"E76.3.0.3")])],"isStart":true}),makeQuery(id+"F9.opExtrude","CAP_FACE",FACE,{"disambiguationData":[OSD([sQuery(id+"F8.wireOp",EDGE,"E76.4.0.0"),sQuery(id+"F8.wireOp",EDGE,"E76.4.0.1"),sQuery(id+"F8.wireOp",EDGE,"E76.4.0.2"),sQuery(id+"F8.wireOp",EDGE,"E76.4.0.3")])],"isStart":true}),makeQuery(id+"F9.opExtrude","CAP_FACE",FACE,{"disambiguationData":[OSD([sQuery(id+"F8.wireOp",EDGE,"E76.5.0.0"),sQuery(id+"F8.wireOp",EDGE,"E76.5.0.1"),sQuery(id+"F8.wireOp",EDGE,"E76.5.0.2"),sQuery(id+"F8.wireOp",EDGE,"E76.5.0.3")])],"isStart":true}),makeQuery(id+"F9.opExtrude","CAP_FACE",FACE,{"disambiguationData":[OSD([sQuery(id+"F8.wireOp",EDGE,"E76.6.0.0"),sQuery(id+"F8.wireOp",EDGE,"E76.6.0.1"),sQuery(id+"F8.wireOp",EDGE,"E76.6.0.2"),sQuery(id+"F8.wireOp",EDGE,"E76.6.0.3")])],"isStart":true}),makeQuery(id+"F9.opExtrude","CAP_FACE",FACE,{"disambiguationData":[OSD([sQuery(id+"F8.wireOp",EDGE,"E76.7.0.0"),sQuery(id+"F8.wireOp",EDGE,"E76.7.0.1"),sQuery(id+"F8.wireOp",EDGE,"E76.7.0.2"),sQuery(id+"F8.wireOp",EDGE,"E76.7.0.3")])],"isStart":true})]});
            var sketch = newSketch(context, id + "F10", { "sketchPlane" : qUnion([Q0])});
            skLineSegment(sketch, "E77.bottom", {"start": v(116.2, -90) * mm, "end": v(114, -90) * mm});
            skLineSegment(sketch, "E77.top", {"start": v(116.2, -96.2) * mm, "end": v(114, -96.2) * mm});
            skLineSegment(sketch, "E77.left", {"start": v(116.2, -90) * mm, "end": v(116.2, -96.2) * mm});
            skLineSegment(sketch, "E77.right", {"start": v(114, -90) * mm, "end": v(114, -96.2) * mm});
            skSolve(sketch);
        }
        {
            var Q0;
            Q0 = qSketchRegion(id + "F10", true);
            extrude(context, id + "F11", {"entities" : qUnion([Q0]), "operationType" : NewBodyOperationType.ADD, "oppositeDirection" : true, "depth" : 6.2 * mm, "offsetDistance" : 25 * mm});
        }
    });
